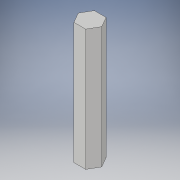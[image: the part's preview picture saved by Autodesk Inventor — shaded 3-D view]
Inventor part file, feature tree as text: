
AUTODESK INVENTOR PART (.ipt)
format: ipt  version: 2019 (Build 230136000, 136)  size: 95,744 bytes
history: native  units: in
note: dims shown in document units (in); Inventor stores cm internally (conversion verified against a paired STEP export)
features: extrude x1, sketch x1
ambient origin geometry x8: Origin, YZ Plane, XZ Plane, XY Plane, X Axis, Y Axis, Z Axis, Center Point
bodies: Solid1 (feature_tree)
feature tree (2):
  extrude  "Extrusion1"  Depth=0.29in
  sketch  "Sketch1"  dims[d1=3.0in d2=0.0in d3=0.29in]
